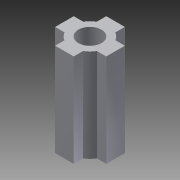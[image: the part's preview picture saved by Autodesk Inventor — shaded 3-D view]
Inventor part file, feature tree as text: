
AUTODESK INVENTOR PART (.ipt)
format: ipt  version: 2015 (Build 190159000, 159)  size: 101,888 bytes
history: native  units: mm
features: sketch x2, extrude x2, other x1, plane x1, hole x1
ambient origin geometry x8: Origin, YZ Plane, XZ Plane, XY Plane, X Axis, Y Axis, Z Axis, Center Point
bodies: Body1 (feature_tree)
feature tree (7):
  other  "Sólido1"
  sketch  "Boceto3"  dims[d2=5.5mm d3=2.0mm d6=2.5mm d7=6.0mm d8=4.0mm d9=2.0mm d10=90.0deg d11=9.0mm d12=20.594885mm d13=4.0mm d14=10.0mm d15=0.0mm d16=10.0mm d17=0.0mm]
  sketch  "Boceto1"  dims[d0=2.0mm d1=5.5mm]
  plane  "Plano de trabajo1"
  extrude  "Extrusión2"  Depth=5.5mm
  extrude  "Extrusión3"  Depth=2.0mm
  hole  "Agujero1"  [1 undecoded]
note: 1 required parameter value undecoded (feature->parameter linkage not recoverable at this tier; creation-order binding heuristic only, values carry confidence <= 0.55)
